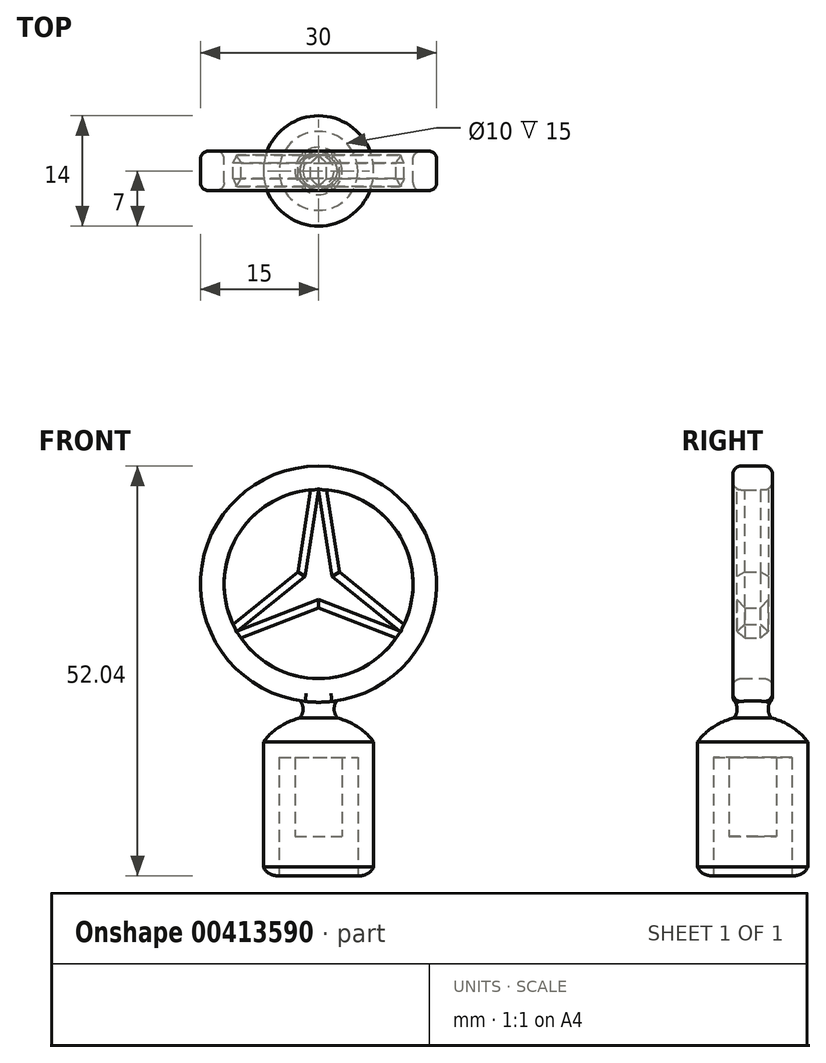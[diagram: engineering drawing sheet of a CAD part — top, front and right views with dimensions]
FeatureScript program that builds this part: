
annotation { "Feature Type Name" : "Feature", "Feature Type Description" : "" }
export const myFeature = defineFeature(function(context is Context, id is Id, definition is map)
    precondition{}
    {
        {
            var Q0;
            Q0=qCreatedBy(makeId("Front.planeOp"),FACE);
            var sketch = newSketch(context, id + "F0", { "sketchPlane" : qUnion([Q0])});
            skLineSegment(sketch, "E0", {"start": v(0, 0) * mm, "end": v(-3, 0) * mm});
            skLineSegment(sketch, "E1", {"start": v(-3, 0) * mm, "end": v(-3, 10) * mm});
            skLineSegment(sketch, "E2", {"start": v(-3, 10) * mm, "end": v(-5, 10) * mm});
            skLineSegment(sketch, "E3", {"start": v(-5, 10) * mm, "end": v(-5, -5) * mm});
            skLineSegment(sketch, "E4", {"start": v(-7, -3.91) * mm, "end": v(-7, 12) * mm});
            skArc(sketch, "E5", {"start": v(-7, -3.91) * mm, "mid": v(-6.18, -4.79) * mm, "end": v(-5, -5) * mm});
            skArc(sketch, "E6", {"start": v(-2.4, 15) * mm, "mid": v(-4.97, 13.9) * mm, "end": v(-7, 12) * mm});
            skArc(sketch, "E7", {"start": v(-2.4, 15) * mm, "mid": v(-1.98, 16.09) * mm, "end": v(-2.32, 17.2) * mm});
            skPoint(sketch, "E8.orphan", {"position": v(0, 15.2) * mm});
            skCircle(sketch, "E9", {"center": v(0, 32.02) * mm, "radius": 15 * mm});
            skCircle(sketch, "E10", {"center": v(0, 32.02) * mm, "radius": 12 * mm});
            skPoint(sketch, "E11", {"position": v(12, 32.02) * mm});
            skPoint(sketch, "E12", {"position": v(15, 32.02) * mm});
            skPoint(sketch, "E13", {"position": v(0, 44.02) * mm});
            skPoint(sketch, "E14.end.orphan", {"position": v(0, 18.92) * mm});
            skPoint(sketch, "E15.end.orphan", {"position": v(-4, 18.44) * mm});
            skPoint(sketch, "E16.start.orphan", {"position": v(-4.77, 17.8) * mm});
            skPoint(sketch, "E17", {"position": v(0, 17.02) * mm});
            skLineSegment(sketch, "E18", {"start": v(0, 44.02) * mm, "end": v(0, 20.02) * mm, "construction": true});
            skLineSegment(sketch, "E19", {"start": v(0, 32.02) * mm, "end": v(-10.4, 26.02) * mm, "construction": true});
            skLineSegment(sketch, "E20", {"start": v(0, 32.02) * mm, "end": v(10.4, 26.02) * mm, "construction": true});
            skPoint(sketch, "E21", {"position": v(-10.4, 26.02) * mm});
            skPoint(sketch, "E22", {"position": v(10.4, 26.02) * mm});
            skLineSegment(sketch, "E23", {"start": v(-1, 43.98) * mm, "end": v(-2.64, 33.55) * mm});
            skLineSegment(sketch, "E24", {"start": v(-2.64, 33.55) * mm, "end": v(-10.86, 26.9) * mm});
            skLineSegment(sketch, "E25", {"start": v(0, 32.02) * mm, "end": v(-2.64, 33.55) * mm, "construction": true});
            skLineSegment(sketch, "E26.MirrorCS", {"start": v(1, 43.98) * mm, "end": v(2.64, 33.55) * mm});
            skLineSegment(sketch, "E27.MirrorCS", {"start": v(2.64, 33.55) * mm, "end": v(10.86, 26.9) * mm});
            skLineSegment(sketch, "E28", {"start": v(-9.86, 25.18) * mm, "end": v(0, 28.97) * mm});
            skLineSegment(sketch, "E29", {"start": v(0, 28.97) * mm, "end": v(9.86, 25.18) * mm});
            skLineSegment(sketch, "E30", {"start": v(-2.32, 17.2) * mm, "end": v(0, 18.92) * mm});
            skLineSegment(sketch, "E31", {"start": v(0, 0) * mm, "end": v(0, 18.92) * mm});
            skSolve(sketch);
        }
        {
            var Q0;
            {var subQ1=sQuery(id+"F0.wireOp",EDGE,"E0");Q0=makeQuery(id+"F0.imprint","IMPRINT",FACE,{"disambiguationData":[TD([[makeQuery(id+"F0.imprint","IMPRINT",EDGE,{"derivedFrom":subQ1}),-1.0]])]});}
            var Q1;
            Q1=sQuery(id+"F0.wireOp",EDGE,"E31");
            revolve(context, id + "F1", {"entities" : qUnion([Q0]), "axis" : qUnion([Q1]), "revolveType" : RevolveType.FULL});
        }
        {
            var Q0;
            {var subQ0=sQuery(id+"F0.wireOp",EDGE,"E30");Q0=makeQuery(id+"F0.imprint","IMPRINT",FACE,{"disambiguationData":[TD([[makeQuery(id+"F0.imprint","IMPRINT",EDGE,{"derivedFrom":subQ0}),-1.0]])]});}
            var Q1;
            {var subQ4=sQuery(id+"F0.wireOp",EDGE,"E30");Q1=makeQuery(id+"F0.imprint","IMPRINT",FACE,{"disambiguationData":[TD([[makeQuery(id+"F0.imprint","IMPRINT",EDGE,{"derivedFrom":subQ4}),1.0]])]});}
            extrude(context, id + "F2", {"entities" : qUnion([Q0, Q1]), "operationType" : NewBodyOperationType.ADD, "depth" : 2.5 * mm, "hasSecondDirection" : true, "secondDirectionOppositeDirection" : true, "secondDirectionDepth" : 2.5 * mm});
        }
        {
            var Q0;
            {var subQ0=sQuery(id+"F0.wireOp",EDGE,"E23");Q0=makeQuery(id+"F0.imprint","IMPRINT",FACE,{"disambiguationData":[TD([[makeQuery(id+"F0.imprint","IMPRINT",EDGE,{"derivedFrom":subQ0}),1.0]])]});}
            extrude(context, id + "F3", {"entities" : qUnion([Q0]), "operationType" : NewBodyOperationType.ADD, "depth" : 2 * mm, "hasSecondDirection" : true, "secondDirectionOppositeDirection" : true, "secondDirectionDepth" : 2 * mm});
        }
        {
            var Q0;
            Q0=makeQuery(id+"F3.opExtrude","CAP_EDGE",EDGE,{"disambiguationData":[OSD([sQuery(id+"F0.wireOp",EDGE,"E26.MirrorCS")])],"isStart":true});
            var Q1;
            Q1=makeQuery(id+"F3.opExtrude","CAP_EDGE",EDGE,{"disambiguationData":[OSD([sQuery(id+"F0.wireOp",EDGE,"E23")])],"isStart":true});
            var Q2;
            Q2=makeQuery(id+"F3.opExtrude","CAP_EDGE",EDGE,{"disambiguationData":[OSD([sQuery(id+"F0.wireOp",EDGE,"E24")])],"isStart":true});
            var Q3;
            Q3=makeQuery(id+"F3.opExtrude","CAP_EDGE",EDGE,{"disambiguationData":[OSD([sQuery(id+"F0.wireOp",EDGE,"E28")])],"isStart":true});
            var Q4;
            Q4=makeQuery(id+"F3.opExtrude","CAP_EDGE",EDGE,{"disambiguationData":[OSD([sQuery(id+"F0.wireOp",EDGE,"E29")])],"isStart":true});
            var Q5;
            Q5=makeQuery(id+"F3.opExtrude","CAP_EDGE",EDGE,{"disambiguationData":[OSD([sQuery(id+"F0.wireOp",EDGE,"E27.MirrorCS")])],"isStart":true});
            var Q6;
            Q6=makeQuery(id+"F3.opExtrude","CAP_EDGE",EDGE,{"disambiguationData":[OSD([sQuery(id+"F0.wireOp",EDGE,"E27.MirrorCS")])],"isStart":false});
            var Q7;
            Q7=makeQuery(id+"F3.opExtrude","CAP_EDGE",EDGE,{"disambiguationData":[OSD([sQuery(id+"F0.wireOp",EDGE,"E26.MirrorCS")])],"isStart":false});
            var Q8;
            Q8=makeQuery(id+"F3.opExtrude","CAP_EDGE",EDGE,{"disambiguationData":[OSD([sQuery(id+"F0.wireOp",EDGE,"E23")])],"isStart":false});
            var Q9;
            Q9=makeQuery(id+"F3.opExtrude","CAP_EDGE",EDGE,{"disambiguationData":[OSD([sQuery(id+"F0.wireOp",EDGE,"E29")])],"isStart":false});
            var Q10;
            Q10=makeQuery(id+"F3.opExtrude","CAP_EDGE",EDGE,{"disambiguationData":[OSD([sQuery(id+"F0.wireOp",EDGE,"E28")])],"isStart":false});
            var Q11;
            Q11=makeQuery(id+"F3.opExtrude","CAP_EDGE",EDGE,{"disambiguationData":[OSD([sQuery(id+"F0.wireOp",EDGE,"E24")])],"isStart":false});
            chamfer(context, id + "F4", {"entities" : qUnion([Q0, Q1, Q2, Q3, Q4, Q5, Q6, Q7, Q8, Q9, Q10, Q11]), "width" : 1 * mm, "tangentPropagation" : true});
        }
        {
            var Q0;
            Q0=makeQuery(id+"F2.opExtrude","CAP_EDGE",EDGE,{"disambiguationData":[OSD([sQuery(id+"F0.wireOp",EDGE,"E9")])],"isStart":false});
            var Q1;
            Q1=makeQuery(id+"F2.opExtrude","CAP_EDGE",EDGE,{"disambiguationData":[OSD([sQuery(id+"F0.wireOp",EDGE,"E10")])],"isStart":false});
            var Q2;
            Q2=makeQuery(id+"F2.opExtrude","CAP_EDGE",EDGE,{"disambiguationData":[OSD([sQuery(id+"F0.wireOp",EDGE,"E10")])],"isStart":true});
            var Q3;
            Q3=makeQuery(id+"F2.opExtrude","CAP_EDGE",EDGE,{"disambiguationData":[OSD([sQuery(id+"F0.wireOp",EDGE,"E9")])],"isStart":true});
            fillet(context, id + "F5", {"entities" : qUnion([Q0, Q1, Q2, Q3]), "radius" : 1 * mm, "tangentPropagation" : true, "allowEdgeOverflow" : false});
        }
    });
